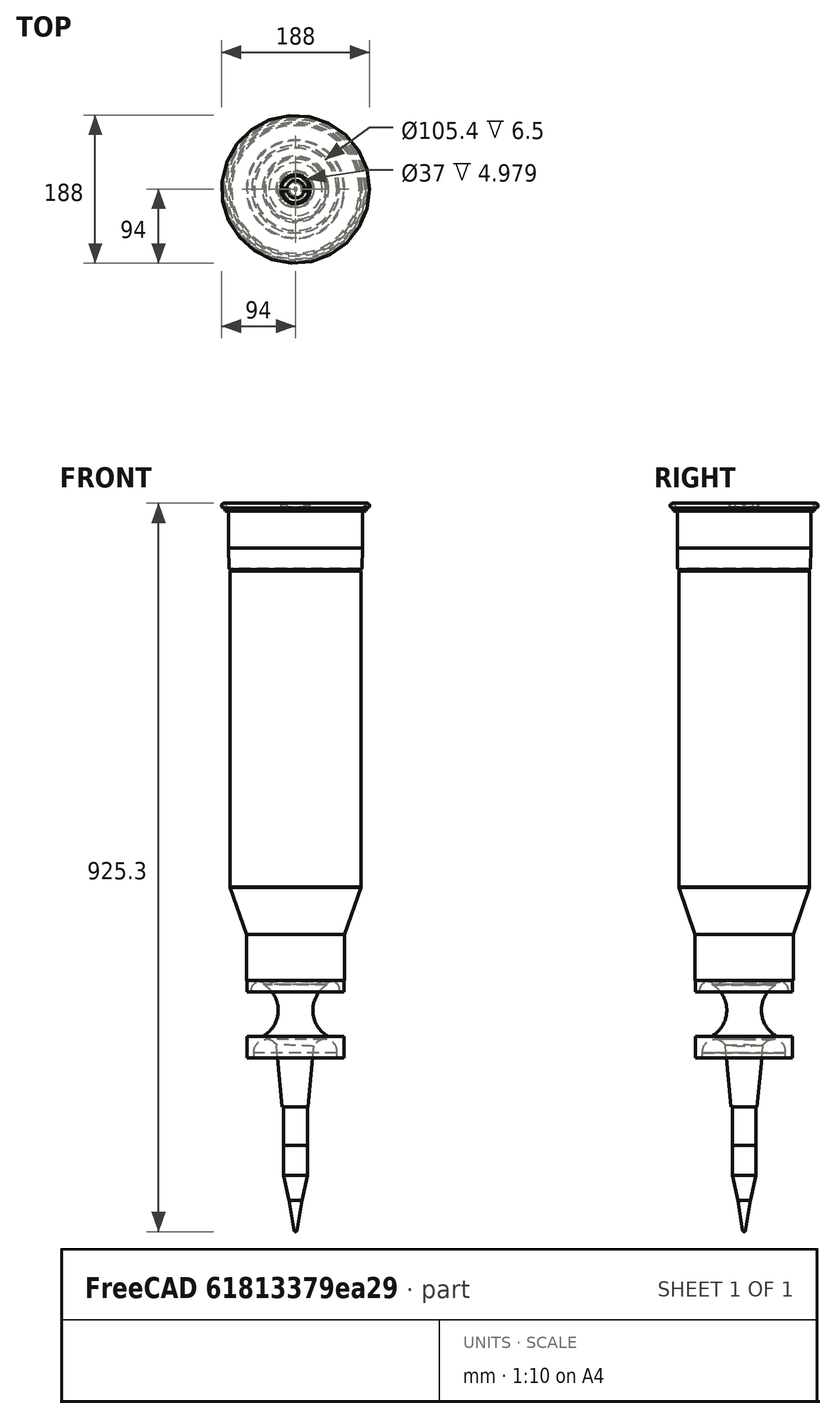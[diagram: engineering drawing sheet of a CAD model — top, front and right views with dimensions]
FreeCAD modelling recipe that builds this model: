
FCSTD DOCUMENT  (FreeCAD 0.19R24291 (Git))
Label: БОПС снаряд M829A1 120 mm
License: All rights reserved
LicenseURL: http://en.wikipedia.org/wiki/All_rights_reserved
objects: Part::Cylinder×20, Part::Cut×13, Part::Cone×7, Part::Torus×4, Part::MultiFuse×4, Part::FeaturePython×2, Part::Box×2, Part::MultiCommon×2, Part::Sphere×2, Part::Fillet×1, App::MeasureDistance×1
note: 57 computed .brp shape members not serialized (recipe doc carries the construction recipe); baked Part::Feature solids carry a one-line shape summary decoded from their .brp

FEATURE [Part::Cylinder] Cylinder001  label="Задний обод"
  Angle = 360
  AttacherType = Attacher::AttachEngine3D
  Height = 5.9788
  Placement = pos=(0,0,978) rot=(0,0,1;0rad)
  Radius = 91
FEATURE [Part::Cylinder] Cylinder002  label="Задний обод1"
  Angle = 360
  AttacherType = Attacher::AttachEngine3D
  Height = 4.3
  Placement = pos=(0,0,974) rot=(0,0,1;0rad)
  Radius = 89.5
FEATURE [Part::Torus] Torus  label="Тор"
  Angle1 = -180
  Angle2 = 180
  Angle3 = 360
  AttacherType = Attacher::AttachEngine3D
  Placement = pos=(0,0,981) rot=(0,0,1;0rad)
  Radius1 = 91
  Radius2 = 3
FEATURE [Part::Cylinder] Cylinder003  label="Цилиндр"
  Angle = 360
  AttacherType = Attacher::AttachEngine3D
  Height = 5
  Placement = pos=(0,0,979) rot=(0,0,1;0rad)
  Radius = 18.5
FEATURE [Part::Cut] Cut001
  Base = -> Cylinder001
  Tool = -> Cylinder003
FEATURE [Part::Cylinder] Cylinder004  label="Цилиндр001"
  Angle = 360
  AttacherType = Attacher::AttachEngine3D
  Height = 5
  Placement = pos=(0,0,1273) rot=(0,0,1;0rad)
  Radius = 17.5
FEATURE [Part::FeaturePython] Tube001  # WARN: FeaturePython — macro-defined, semantics opaque (R4)
  AttacherType = Attacher::AttachEngine3D
  Height = 2.5
  InnerRadius = 11
  OuterRadius = 17.5
  Placement = pos=(0,0,1325) rot=(0,0,1;0rad)
FEATURE [Part::Box] Box  label="Куб"
  AttacherType = Attacher::AttachEngine3D
  Height = 10
  Length = 10
  Placement = pos=(8.31,4.96,1332) rot=(-0.360216,0.860516,0.360216;1.71775rad)
  Width = 4
FEATURE [Part::MultiCommon] Common
  Placement = pos=(0,0,-49) rot=(0,0,1;0rad)
  Shapes = -> [Box,Tube001]
FEATURE [Part::Cut] Cut002
  Base = -> Cylinder004
  Tool = -> Common
FEATURE [Part::Box] Box001  label="Куб001"
  AttacherType = Attacher::AttachEngine3D
  Height = 10
  Length = 10
  Placement = pos=(-11.3596,-14.9674,1331.93) rot=(-0.360216,0.860516,0.360216;1.71775rad)
  Width = 4
FEATURE [Part::FeaturePython] Tube002  # WARN: FeaturePython — macro-defined, semantics opaque (R4)
  AttacherType = Attacher::AttachEngine3D
  Height = 2.5
  InnerRadius = 11
  OuterRadius = 17.5
  Placement = pos=(0,0,1325) rot=(0,0,1;0rad)
FEATURE [Part::MultiCommon] Common001
  Placement = pos=(0,0,-48.5) rot=(0,0,1;0rad)
  Shapes = -> [Tube002,Box001]
FEATURE [Part::Cut] Cut003  label="капсуль"
  Base = -> Cut002
  Placement = pos=(0,0,-294.3) rot=(0,0,-1;0.785398rad)
  Tool = -> Common001
FEATURE [Part::Cylinder] Cylinder005  label="Цилиндр002"
  Angle = 360
  AttacherType = Attacher::AttachEngine3D
  Height = 5
  Placement = pos=(0,0,979) rot=(0,0,1;0rad)
  Radius = 18.5
FEATURE [Part::Cylinder] Cylinder006  label="Цилиндр003"
  Angle = 360
  AttacherType = Attacher::AttachEngine3D
  Height = 47
  Placement = pos=(0,0,927) rot=(0,0,1;0rad)
  Radius = 85
FEATURE [Part::Cut] Cut
  Base = -> Cut001
  Tool = -> Cylinder005
FEATURE [Part::Cut] Cut004
  Base = -> Cut
  Tool = -> Cylinder003
FEATURE [Part::Cone] Cone  label="Конус"
  Angle = 360
  AttacherType = Attacher::AttachEngine3D
  Height = 27
  Placement = pos=(0,0,900.03) rot=(0,0,1;0rad)
  Radius1 = 84.5
  Radius2 = 85
FEATURE [Part::Fillet] Fillet
  Base = -> Cone
  Edges = 1 edges r=2: [Edge3]
FEATURE [Part::Cone] Cone001  label="Конус001"
  Angle = 360
  AttacherType = Attacher::AttachEngine3D
  Height = 3
  Placement = pos=(0,0,898.1) rot=(0,0,1;0rad)
  Radius1 = 83
  Radius2 = 81
FEATURE [Part::Cylinder] Cylinder007  label="Задний обод002"
  Angle = 360
  AttacherType = Attacher::AttachEngine3D
  Height = 4.3
  Placement = pos=(0,0,0.46) rot=(0,0,1;0rad)
  Radius = 89.5
FEATURE [Part::Cylinder] Cylinder  label="Цилиндр004"
  Angle = 360
  AttacherType = Attacher::AttachEngine3D
  Height = 10
  Radius = 85
FEATURE [Part::Cut] Cut005
  Base = -> Cylinder007
  Placement = pos=(0,0,924.89) rot=(0,0,1;0rad)
  Tool = -> Cylinder
FEATURE [Part::Cut] Cut006
  Base = -> Fillet
  Tool = -> Cut005
FEATURE [Part::Cylinder] Cylinder008  label="Задний обод003"
  Angle = 360
  AttacherType = Attacher::AttachEngine3D
  Height = 4.3
  Placement = pos=(0,0,0.46) rot=(0,0,1;0rad)
  Radius = 89.5
FEATURE [Part::Cut] Cut007
  Base = -> Cylinder006
  Tool = -> Cylinder008
FEATURE [Part::Cylinder] Cylinder009  label="Цилиндр005"
  Angle = 360
  AttacherType = Attacher::AttachEngine3D
  Height = 402
  Placement = pos=(0,0,496.189) rot=(0,0,1;0rad)
  Radius = 83
FEATURE [Part::Cone] Cone002  label="Конус002"
  Angle = 360
  AttacherType = Attacher::AttachEngine3D
  Height = 60
  Placement = pos=(0,0,436.367) rot=(0,0,1;0rad)
  Radius1 = 62.5
  Radius2 = 83
FEATURE [Part::Cylinder] Cylinder010  label="Цилиндр006"
  Angle = 360
  AttacherType = Attacher::AttachEngine3D
  Height = 59
  Placement = pos=(0,0,377.76) rot=(0,0,1;0rad)
  Radius = 62.5
FEATURE [Part::Cylinder] Cylinder011  label="Цилиндр007"
  Angle = 360
  AttacherType = Attacher::AttachEngine3D
  Height = 15
  Placement = pos=(0,0,362.948) rot=(0,0,1;0rad)
  Radius = 61.5
FEATURE [Part::Torus] Torus002  label="Тор002"
  Angle1 = -180
  Angle2 = 180
  Angle3 = 360
  AttacherType = Attacher::AttachEngine3D
  Placement = pos=(0,0,366.115) rot=(0,0,1;0rad)
  Radius1 = 46
  Radius2 = 10
FEATURE [Part::Cut] Cut008
  Base = -> Cylinder011
  Tool = -> Torus002
FEATURE [Part::Sphere] Sphere  label="Сфера"
  Angle1 = -90
  Angle2 = 90
  Angle3 = 360
  AttacherType = Attacher::AttachEngine3D
  Placement = pos=(0,0,321.679) rot=(0,0,1;0rad)
  Radius = 61
FEATURE [Part::Cut] Cut009
  Base = -> Cut008
  Tool = -> Sphere
FEATURE [Part::Cylinder] Cylinder013  label="Цилиндр009"
  Angle = 360
  AttacherType = Attacher::AttachEngine3D
  Height = 6.5
  Placement = pos=(0,0,300.088) rot=(0,0,1;0rad)
  Radius = 61.5
FEATURE [Part::Cylinder] Cylinder014  label="Цилиндр010"
  Angle = 360
  AttacherType = Attacher::AttachEngine3D
  Height = 33.5
  Placement = pos=(0,0,162.088) rot=(0,0,1;0rad)
  Radius = 40
FEATURE [Part::Cone] Cone005  label="Конус005"
  Angle = 360
  AttacherType = Attacher::AttachEngine3D
  Height = 33.5
  Placement = pos=(-2e-14,0,163) rot=(0,1,0;3.14159rad)
  Radius1 = 40
  Radius2 = 48
FEATURE [Part::Torus] Torus004  label="Тор004"
  Angle1 = -180
  Angle2 = 180
  Angle3 = 360
  AttacherType = Attacher::AttachEngine3D
  Placement = pos=(0,0,163) rot=(0,0,1;0rad)
  Radius1 = 60
  Radius2 = 38
FEATURE [Part::MultiFuse] Fusion001
  Shapes = -> [Cylinder014,Cone005]
FEATURE [Part::Cut] Cut012
  Base = -> Fusion001
  Placement = pos=(0,0,177) rot=(0,0,1;0rad)
  Tool = -> Torus004
FEATURE [Part::Cylinder] Cylinder015  label="Цилиндр011"
  Angle = 360
  AttacherType = Attacher::AttachEngine3D
  Height = 14
  Placement = pos=(0,0,286.088) rot=(0,0,1;0rad)
  Radius = 61.5
FEATURE [Part::Cylinder] Cylinder016  label="Цилиндр012"
  Angle = 360
  AttacherType = Attacher::AttachEngine3D
  Height = 6.5
  Placement = pos=(0,0,-225.912) rot=(0,0,1;0rad)
  Radius = 61.5
FEATURE [Part::Torus] Torus005  label="Тор005"
  Angle1 = -180
  Angle2 = 180
  Angle3 = 360
  AttacherType = Attacher::AttachEngine3D
  Placement = pos=(0,0,-5) rot=(0,0,1;0rad)
  Radius1 = 37.2
  Radius2 = 15.5
FEATURE [Part::MultiFuse] Fusion
  Placement = pos=(0,0,-292.5) rot=(0,0,1;0rad)
  Shapes = -> [Cylinder015,Cylinder013]
FEATURE [Part::Cut] Cut013
  Base = -> Fusion
  Tool = -> Torus005
FEATURE [Part::Cone] Cone006  label="Конус006"
  Angle = 360
  AttacherType = Attacher::AttachEngine3D
  Height = 80
  Placement = pos=(-0.5,0,-75.5) rot=(0,0,1;0rad)
  Radius1 = 16.5
  Radius2 = 24
FEATURE [Part::Cylinder] Cylinder017  label="Цилиндр013"
  Angle = 360
  AttacherType = Attacher::AttachEngine3D
  Height = 10
  Placement = pos=(0,0,-227) rot=(0,0,1;0rad)
  Radius = 52.7
FEATURE [Part::Cut] Cut014
  Base = -> Cylinder016
  Placement = pos=(0,0,213) rot=(0,0,1;0rad)
  Tool = -> Cylinder017
FEATURE [Part::MultiFuse] Fusion002
  Placement = pos=(0,0,292.5) rot=(0,0,1;0rad)
  Shapes = -> [Cone006,Cut013,Cut014]
FEATURE [Part::Cylinder] Cylinder018  label="Цилиндр014"
  Angle = 360
  AttacherType = Attacher::AttachEngine3D
  Height = 49
  Placement = pos=(0,0,168.5) rot=(0,0,1;0rad)
  Radius = 15
FEATURE [Part::Cylinder] Cylinder019  label="Цилиндр015"
  Angle = 360
  AttacherType = Attacher::AttachEngine3D
  Height = 38
  Placement = pos=(0,0,130.5) rot=(0,0,1;0rad)
  Radius = 15
FEATURE [Part::Cone] Cone007  label="Конус007"
  Angle = 360
  AttacherType = Attacher::AttachEngine3D
  Height = 32
  Placement = pos=(0,0,98.5) rot=(0,0,1;0rad)
  Radius1 = 8
  Radius2 = 15
FEATURE [Part::Cone] Cone008  label="Конус008"
  Angle = 360
  AttacherType = Attacher::AttachEngine3D
  Height = 38
  Placement = pos=(0,0,60.5) rot=(0,0,1;0rad)
  Radius1 = 2
  Radius2 = 8
FEATURE [Part::Sphere] Sphere001  label="Сфера001"
  Angle1 = -90
  Angle2 = 0
  Angle3 = 360
  AttacherType = Attacher::AttachEngine3D
  Placement = pos=(0,0,60.7) rot=(0,0,1;0rad)
  Radius = 2
FEATURE [Part::Cylinder] Cylinder020  label="Цилиндр016"
  Angle = 360
  AttacherType = Attacher::AttachEngine3D
  Height = 10
  Placement = pos=(0,0,973.8) rot=(0,0,1;0rad)
  Radius = 11.1
FEATURE [Part::MultiFuse] Fusion003
  Shapes = -> [Cut009,Cut012,Fusion002]
FEATURE [App::MeasureDistance] Distance  label="Distance: 8,59 mm"
  Distance = 8.59435
  P1 = (59.668,-13.6211,-6.41237)
  P2 = (51.2327,-11.975,-6.41237)
